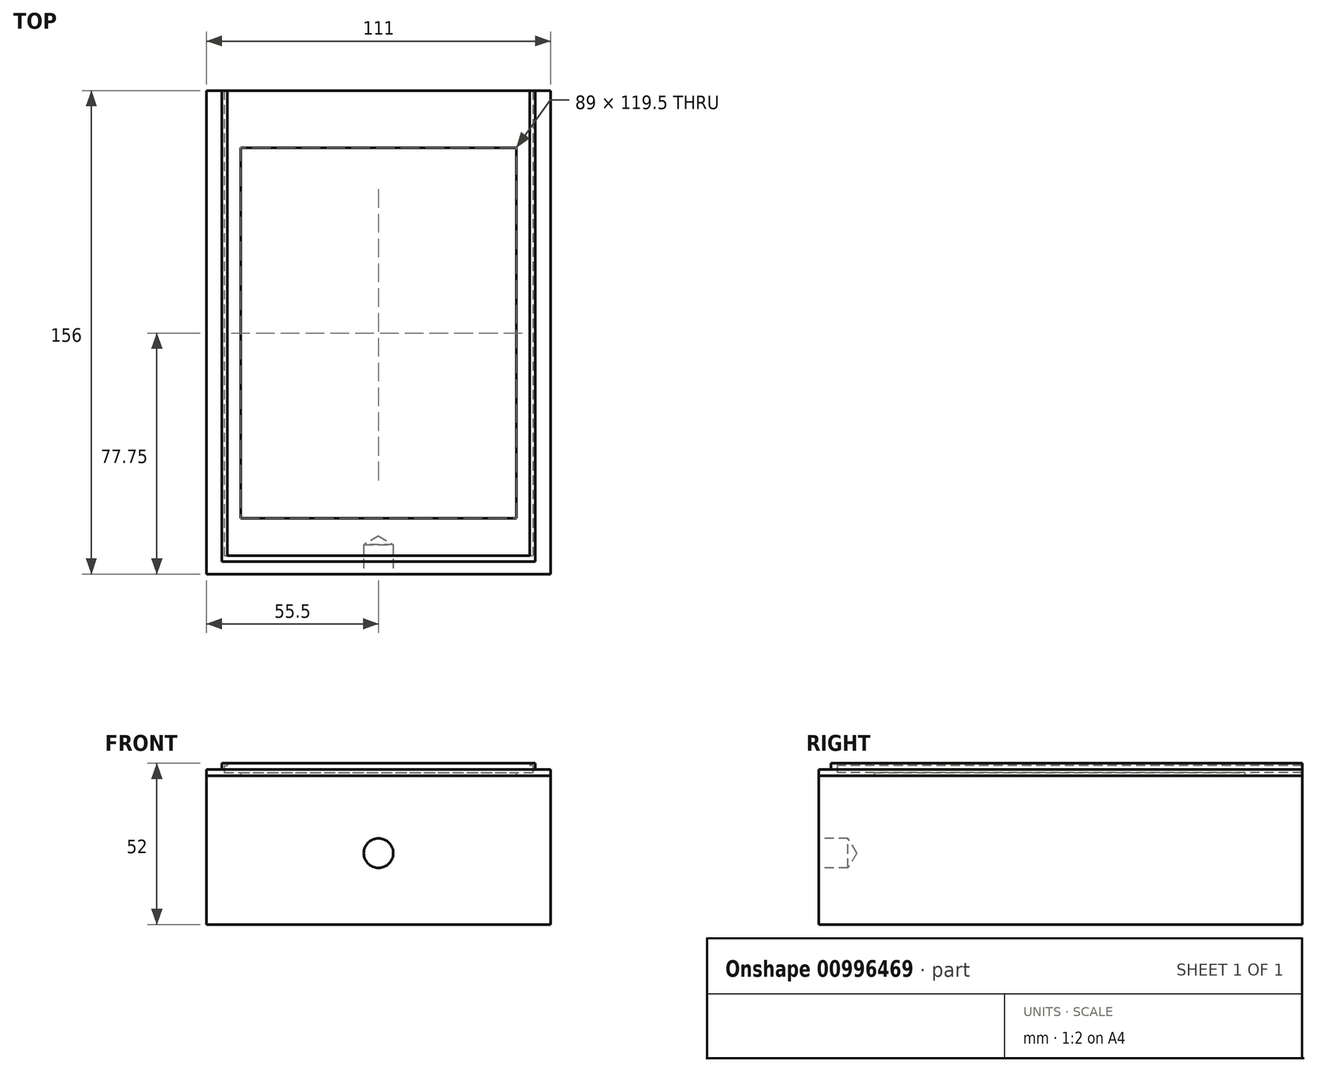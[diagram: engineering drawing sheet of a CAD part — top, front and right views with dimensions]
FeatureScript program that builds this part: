
annotation { "Feature Type Name" : "Feature", "Feature Type Description" : "" }
export const myFeature = defineFeature(function(context is Context, id is Id, definition is map)
    precondition{}
    {
        {
            var Q0;
            Q0=qCreatedBy(makeId("Top.planeOp"),FACE);
            var sketch = newSketch(context, id + "F0", { "sketchPlane" : qUnion([Q0])});
            skLineSegment(sketch, "E0.bottom", {"start": v(-44.5, -63) * mm, "end": v(44.5, -63) * mm});
            skLineSegment(sketch, "E0.top", {"start": v(-44.5, 56.5) * mm, "end": v(44.5, 56.5) * mm});
            skLineSegment(sketch, "E0.left", {"start": v(-44.5, -63) * mm, "end": v(-44.5, 56.5) * mm});
            skLineSegment(sketch, "E0.right", {"start": v(44.5, -63) * mm, "end": v(44.5, 56.5) * mm});
            skLineSegment(sketch, "E1.bottom", {"start": v(-48.75, 75) * mm, "end": v(48.75, 75) * mm});
            skLineSegment(sketch, "E1.top", {"start": v(-48.75, -75) * mm, "end": v(48.75, -75) * mm});
            skLineSegment(sketch, "E1.left", {"start": v(-48.75, 75) * mm, "end": v(-48.75, -75) * mm});
            skLineSegment(sketch, "E1.right", {"start": v(48.75, 75) * mm, "end": v(48.75, -75) * mm});
            skLineSegment(sketch, "E2", {"start": v(-48.75, 0) * mm, "end": v(48.75, 0) * mm, "construction": true});
            skLineSegment(sketch, "E3.bottom", {"start": v(-50.5, 75) * mm, "end": v(50.5, 75) * mm});
            skLineSegment(sketch, "E3.top", {"start": v(-50.5, -77) * mm, "end": v(50.5, -77) * mm});
            skLineSegment(sketch, "E3.left", {"start": v(-50.5, 75) * mm, "end": v(-50.5, -77) * mm});
            skLineSegment(sketch, "E3.right", {"start": v(50.5, 75) * mm, "end": v(50.5, -77) * mm});
            skLineSegment(sketch, "E4", {"start": v(0, 75) * mm, "end": v(0, -77) * mm, "construction": true});
            skLineSegment(sketch, "E5", {"start": v(0, -63) * mm, "end": v(0, 56.5) * mm, "construction": true});
            skLineSegment(sketch, "E6.bottom", {"start": v(-55.5, -81) * mm, "end": v(55.5, -81) * mm});
            skLineSegment(sketch, "E6.top", {"start": v(-55.5, 75) * mm, "end": v(55.5, 75) * mm});
            skLineSegment(sketch, "E6.left", {"start": v(-55.5, -81) * mm, "end": v(-55.5, 75) * mm});
            skLineSegment(sketch, "E6.right", {"start": v(55.5, -81) * mm, "end": v(55.5, 75) * mm});
            skSolve(sketch);
        }
        {
            var Q0;
            Q0=makeQuery(id+"F0.imprint","IMPRINT",FACE,{"disambiguationData":[TD([[makeQuery(id+"F0.imprint","IMPRINT",EDGE,{"derivedFrom":sQuery(id+"F0.wireOp",EDGE,"E3.top")}),-1.0]])]});
            var Q1;
            Q1=makeQuery(id+"F0.imprint","IMPRINT",FACE,{"disambiguationData":[TD([[makeQuery(id+"F0.imprint","IMPRINT",EDGE,{"derivedFrom":sQuery(id+"F0.wireOp",EDGE,"E0.bottom")}),-1.0]])]});
            var Q2;
            Q2=makeQuery(id+"F0.imprint","IMPRINT",FACE,{"disambiguationData":[TD([[makeQuery(id+"F0.imprint","IMPRINT",EDGE,{"derivedFrom":sQuery(id+"F0.wireOp",EDGE,"E1.top")}),-1.0]])]});
            extrude(context, id + "F1", {"entities" : qUnion([Q0, Q1, Q2]), "depth" : 1 * mm, "offsetDistance" : 25 * mm, "symmetric" : true});
        }
        {
            var Q0;
            Q0=makeQuery(id+"F1.opExtrude","CAP_FACE",FACE,{"disambiguationData":[OSD([sQuery(id+"F0.wireOp",EDGE,"E0.bottom"),sQuery(id+"F0.wireOp",EDGE,"E0.top"),sQuery(id+"F0.wireOp",EDGE,"E0.left"),sQuery(id+"F0.wireOp",EDGE,"E0.right"),sQuery(id+"F0.wireOp",EDGE,"E6.bottom"),sQuery(id+"F0.wireOp",EDGE,"E6.top"),sQuery(id+"F0.wireOp",EDGE,"E6.left"),sQuery(id+"F0.wireOp",EDGE,"E6.right")])],"isStart":false});
            var sketch = newSketch(context, id + "F2", { "sketchPlane" : qUnion([Q0])});
            skLineSegment(sketch, "E7.bottom", {"start": v(-44.5, -63) * mm, "end": v(44.5, -63) * mm});
            skLineSegment(sketch, "E7.top", {"start": v(-44.5, 56.5) * mm, "end": v(44.5, 56.5) * mm});
            skLineSegment(sketch, "E7.left", {"start": v(-44.5, -63) * mm, "end": v(-44.5, 56.5) * mm});
            skLineSegment(sketch, "E7.right", {"start": v(44.5, -63) * mm, "end": v(44.5, 56.5) * mm});
            skLineSegment(sketch, "E8.bottom", {"start": v(-48.75, 75) * mm, "end": v(48.75, 75) * mm});
            skLineSegment(sketch, "E8.top", {"start": v(-48.75, -75) * mm, "end": v(48.75, -75) * mm});
            skLineSegment(sketch, "E8.left", {"start": v(-48.75, 75) * mm, "end": v(-48.75, -75) * mm});
            skLineSegment(sketch, "E8.right", {"start": v(48.75, 75) * mm, "end": v(48.75, -75) * mm});
            skLineSegment(sketch, "E9", {"start": v(-48.75, 0) * mm, "end": v(48.75, 0) * mm, "construction": true});
            skLineSegment(sketch, "E10.bottom", {"start": v(-50.5, 75) * mm, "end": v(50.5, 75) * mm});
            skLineSegment(sketch, "E10.top", {"start": v(-50.5, -77) * mm, "end": v(50.5, -77) * mm});
            skLineSegment(sketch, "E10.left", {"start": v(-50.5, 75) * mm, "end": v(-50.5, -77) * mm});
            skLineSegment(sketch, "E10.right", {"start": v(50.5, 75) * mm, "end": v(50.5, -77) * mm});
            skLineSegment(sketch, "E11", {"start": v(0, 75) * mm, "end": v(0, -77) * mm, "construction": true});
            skLineSegment(sketch, "E12", {"start": v(0, -63) * mm, "end": v(0, 56.5) * mm, "construction": true});
            skLineSegment(sketch, "E13.bottom", {"start": v(-55.5, -81) * mm, "end": v(55.5, -81) * mm});
            skLineSegment(sketch, "E13.top", {"start": v(-55.5, 75) * mm, "end": v(55.5, 75) * mm});
            skLineSegment(sketch, "E13.left", {"start": v(-55.5, -81) * mm, "end": v(-55.5, 75) * mm});
            skLineSegment(sketch, "E13.right", {"start": v(55.5, -81) * mm, "end": v(55.5, 75) * mm});
            skSolve(sketch);
        }
        {
            var Q0;
            Q0=makeQuery(id+"F2.imprint","IMPRINT",FACE,{"disambiguationData":[TD([[makeQuery(id+"F2.imprint","IMPRINT",EDGE,{"derivedFrom":sQuery(id+"F2.wireOp",EDGE,"E10.top")}),-1.0]])]});
            extrude(context, id + "F3", {"entities" : qUnion([Q0]), "operationType" : NewBodyOperationType.ADD, "depth" : 1 * mm, "offsetDistance" : 25 * mm});
        }
        {
            var Q0;
            Q0=makeQuery(id+"F1.opExtrude","CAP_FACE",FACE,{"disambiguationData":[OSD([sQuery(id+"F0.wireOp",EDGE,"E0.bottom"),sQuery(id+"F0.wireOp",EDGE,"E0.top"),sQuery(id+"F0.wireOp",EDGE,"E0.left"),sQuery(id+"F0.wireOp",EDGE,"E0.right"),sQuery(id+"F0.wireOp",EDGE,"E6.bottom"),sQuery(id+"F0.wireOp",EDGE,"E6.top"),sQuery(id+"F0.wireOp",EDGE,"E6.left"),sQuery(id+"F0.wireOp",EDGE,"E6.right")])],"isStart":false});
            var sketch = newSketch(context, id + "F4", { "sketchPlane" : qUnion([Q0])});
            skLineSegment(sketch, "E14.bottom", {"start": v(-44.5, -63) * mm, "end": v(44.5, -63) * mm});
            skLineSegment(sketch, "E14.top", {"start": v(-44.5, 56.5) * mm, "end": v(44.5, 56.5) * mm});
            skLineSegment(sketch, "E14.left", {"start": v(-44.5, -63) * mm, "end": v(-44.5, 56.5) * mm});
            skLineSegment(sketch, "E14.right", {"start": v(44.5, -63) * mm, "end": v(44.5, 56.5) * mm});
            skLineSegment(sketch, "E15.bottom", {"start": v(-48.75, 75) * mm, "end": v(48.75, 75) * mm});
            skLineSegment(sketch, "E15.top", {"start": v(-48.75, -75) * mm, "end": v(48.75, -75) * mm});
            skLineSegment(sketch, "E15.left", {"start": v(-48.75, 75) * mm, "end": v(-48.75, -75) * mm});
            skLineSegment(sketch, "E15.right", {"start": v(48.75, 75) * mm, "end": v(48.75, -75) * mm});
            skLineSegment(sketch, "E16", {"start": v(-48.75, 0) * mm, "end": v(48.75, 0) * mm, "construction": true});
            skLineSegment(sketch, "E17.bottom", {"start": v(-50.5, 75) * mm, "end": v(50.5, 75) * mm});
            skLineSegment(sketch, "E17.top", {"start": v(-50.5, -77) * mm, "end": v(50.5, -77) * mm});
            skLineSegment(sketch, "E17.left", {"start": v(-50.5, 75) * mm, "end": v(-50.5, -77) * mm});
            skLineSegment(sketch, "E17.right", {"start": v(50.5, 75) * mm, "end": v(50.5, -77) * mm});
            skLineSegment(sketch, "E18", {"start": v(0, 75) * mm, "end": v(0, -77) * mm, "construction": true});
            skLineSegment(sketch, "E19", {"start": v(0, -63) * mm, "end": v(0, 56.5) * mm, "construction": true});
            skLineSegment(sketch, "E20.bottom", {"start": v(-55.5, -81) * mm, "end": v(55.5, -81) * mm});
            skLineSegment(sketch, "E20.top", {"start": v(-55.5, 75) * mm, "end": v(55.5, 75) * mm});
            skLineSegment(sketch, "E20.left", {"start": v(-55.5, -81) * mm, "end": v(-55.5, 75) * mm});
            skLineSegment(sketch, "E20.right", {"start": v(55.5, -81) * mm, "end": v(55.5, 75) * mm});
            skSolve(sketch);
        }
        {
            var Q0;
            Q0=makeQuery(id+"F4.imprint","IMPRINT",FACE,{"disambiguationData":[TD([[makeQuery(id+"F4.imprint","IMPRINT",EDGE,{"derivedFrom":sQuery(id+"F4.wireOp",EDGE,"E15.top")}),-1.0]])]});
            extrude(context, id + "F5", {"entities" : qUnion([Q0]), "operationType" : NewBodyOperationType.ADD, "depth" : 3 * mm, "offsetDistance" : 25 * mm});
        }
        {
            var Q0;
            Q0=makeQuery(id+"F5.opExtrude","SWEPT_FACE",FACE,{"disambiguationData":[OSD([sQuery(id+"F4.wireOp",EDGE,"E15.left")])]});
            var sketch = newSketch(context, id + "F6", { "sketchPlane" : qUnion([Q0])});
            skLineSegment(sketch, "E21.bottom", {"start": v(75, 0.5) * mm, "end": v(-75, 0.5) * mm});
            skLineSegment(sketch, "E21.top", {"start": v(75, 2.75) * mm, "end": v(-75, 2.75) * mm});
            skLineSegment(sketch, "E21.left", {"start": v(75, 0.5) * mm, "end": v(75, 2.75) * mm});
            skLineSegment(sketch, "E21.right", {"start": v(-75, 0.5) * mm, "end": v(-75, 2.75) * mm});
            skSolve(sketch);
        }
        {
            var Q0;
            Q0=makeQuery(id+"F6.imprint","IMPRINT",FACE,{"disambiguationData":[TD([[makeQuery(id+"F6.imprint","IMPRINT",EDGE,{"derivedFrom":sQuery(id+"F6.wireOp",EDGE,"E21.bottom")}),-1.0]])]});
            extrude(context, id + "F7", {"entities" : qUnion([Q0]), "operationType" : NewBodyOperationType.REMOVE, "depth" : -1 * mm, "offsetDistance" : 25 * mm});
        }
        {
            var Q0;
            Q0=makeQuery(id+"F5.opExtrude","SWEPT_FACE",FACE,{"disambiguationData":[OSD([sQuery(id+"F4.wireOp",EDGE,"E15.right")])]});
            var sketch = newSketch(context, id + "F8", { "sketchPlane" : qUnion([Q0])});
            skLineSegment(sketch, "E22.bottom", {"start": v(-75, 0.5) * mm, "end": v(75, 0.5) * mm});
            skLineSegment(sketch, "E22.top", {"start": v(-75, 2.75) * mm, "end": v(75, 2.75) * mm});
            skLineSegment(sketch, "E22.left", {"start": v(-75, 0.5) * mm, "end": v(-75, 2.75) * mm});
            skLineSegment(sketch, "E22.right", {"start": v(75, 0.5) * mm, "end": v(75, 2.75) * mm});
            skSolve(sketch);
        }
        {
            var Q0;
            Q0=makeQuery(id+"F8.imprint","IMPRINT",FACE,{"disambiguationData":[TD([[makeQuery(id+"F8.imprint","IMPRINT",EDGE,{"derivedFrom":sQuery(id+"F8.wireOp",EDGE,"E22.bottom")}),1.0]])]});
            extrude(context, id + "F9", {"entities" : qUnion([Q0]), "operationType" : NewBodyOperationType.REMOVE, "oppositeDirection" : true, "depth" : 1 * mm, "offsetDistance" : 25 * mm});
        }
        {
            var Q0;
            Q0=makeQuery(id+"F3.boolean.opBoolean","MERGE",FACE,{"derivedFrom":[makeQuery(id+"F1.opExtrude","SWEPT_FACE",FACE,{"disambiguationData":[OSD([sQuery(id+"F0.wireOp",EDGE,"E6.bottom")])]}),makeQuery(id+"F3.opExtrude","SWEPT_FACE",FACE,{"disambiguationData":[OSD([sQuery(id+"F2.wireOp",EDGE,"E13.bottom")])]})]});
            var sketch = newSketch(context, id + "F10", { "sketchPlane" : qUnion([Q0])});
            skLineSegment(sketch, "E23.bottom", {"start": v(-55.5, -0.5) * mm, "end": v(55.5, -0.5) * mm});
            skLineSegment(sketch, "E23.top", {"start": v(-55.5, -48.5) * mm, "end": v(55.5, -48.5) * mm});
            skLineSegment(sketch, "E23.left", {"start": v(-55.5, -0.5) * mm, "end": v(-55.5, -48.5) * mm});
            skLineSegment(sketch, "E23.right", {"start": v(55.5, -0.5) * mm, "end": v(55.5, -48.5) * mm});
            skSolve(sketch);
        }
        {
            var Q0;
            Q0=makeQuery(id+"F10.imprint","IMPRINT",FACE,{"disambiguationData":[TD([[makeQuery(id+"F10.imprint","IMPRINT",EDGE,{"derivedFrom":sQuery(id+"F10.wireOp",EDGE,"E23.bottom")}),-1.0]])]});
            extrude(context, id + "F11", {"entities" : qUnion([Q0]), "oppositeDirection" : true, "depth" : 156 * mm, "offsetDistance" : 25 * mm});
        }
        {
            var Q0;
            Q0=makeQuery(id+"F11.opExtrude","CAP_FACE",FACE,{"disambiguationData":[OSD([sQuery(id+"F10.wireOp",EDGE,"E23.bottom"),sQuery(id+"F10.wireOp",EDGE,"E23.top"),sQuery(id+"F10.wireOp",EDGE,"E23.left"),sQuery(id+"F10.wireOp",EDGE,"E23.right")])],"isStart":true});
            var sketch = newSketch(context, id + "F12", { "sketchPlane" : qUnion([Q0])});
            skPoint(sketch, "E24", {"position": v(0, -25.5) * mm});
            skSolve(sketch);
        }
        {
            var Q0;
            Q0=sQuery(id+"F12.wireOp",VERTEX,"E24");
            var Q1;
            Q1=makeQuery(id+"F11.opExtrude","SWEPT_BODY",BODY,{"disambiguationData":[OSD([sQuery(id+"F10.wireOp",EDGE,"E23.bottom"),sQuery(id+"F10.wireOp",EDGE,"E23.top"),sQuery(id+"F10.wireOp",EDGE,"E23.left"),sQuery(id+"F10.wireOp",EDGE,"E23.right")])]});
            hole(context, id + "F13", {"style" : HoleStyle.SIMPLE, "endStyle" : HoleEndStyle.BLIND, "holeDiameter" : 9.53 * mm, "majorDiameter" : 5 * mm, "holeDepth" : 9.5 * mm, "isTappedThrough" : true, "tappedDepth" : 12 * mm, "tapClearance" : 3, "locations" : qUnion([Q0]), "scope" : qUnion([Q1])});
        }
    });
